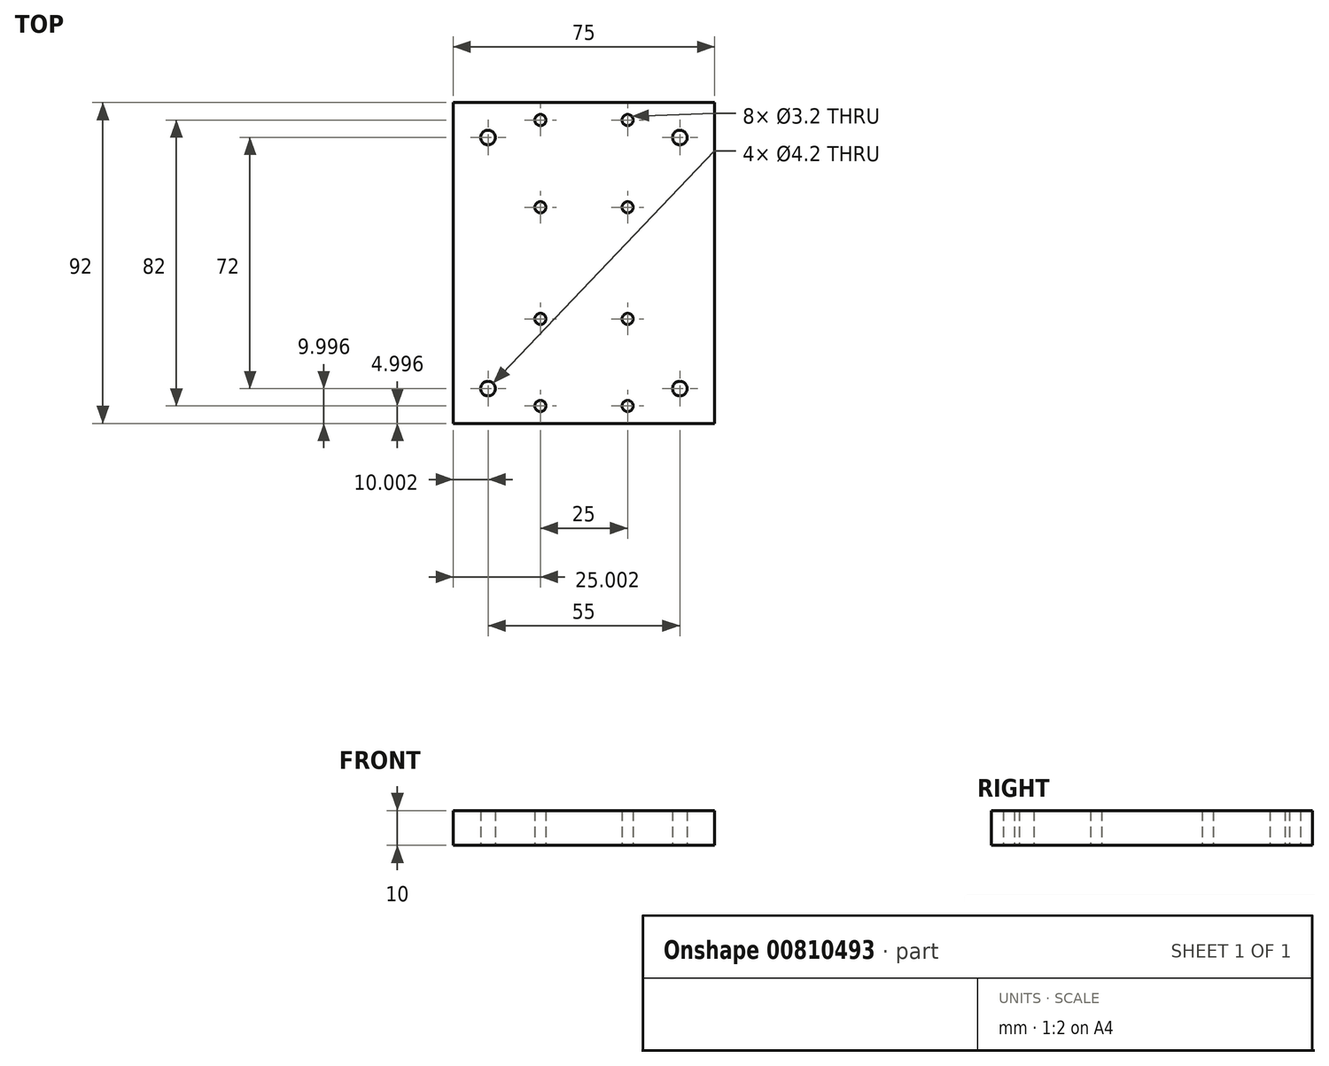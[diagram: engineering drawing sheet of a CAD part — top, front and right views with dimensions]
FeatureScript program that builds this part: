
annotation { "Feature Type Name" : "Feature", "Feature Type Description" : "" }
export const myFeature = defineFeature(function(context is Context, id is Id, definition is map)
    precondition{}
    {
        {
            var Q0;
            Q0=qCreatedBy(makeId("Top.planeOp"),FACE);
            var sketch = newSketch(context, id + "F0", { "sketchPlane" : qUnion([Q0])});
            skLineSegment(sketch, "E0.bottom", {"start": v(-49.76, 39.35) * mm, "end": v(25.24, 39.35) * mm});
            skLineSegment(sketch, "E0.top", {"start": v(-49.76, -52.65) * mm, "end": v(25.24, -52.65) * mm});
            skLineSegment(sketch, "E0.left", {"start": v(-49.76, 39.35) * mm, "end": v(-49.76, -52.65) * mm});
            skLineSegment(sketch, "E0.right", {"start": v(25.24, 39.35) * mm, "end": v(25.24, -52.65) * mm});
            skCircle(sketch, "E1", {"center": v(-39.76, 29.35) * mm, "radius": 2.1 * mm});
            skCircle(sketch, "E2", {"center": v(15.24, 29.35) * mm, "radius": 2.1 * mm});
            skCircle(sketch, "E3", {"center": v(-39.76, -42.65) * mm, "radius": 2.1 * mm});
            skCircle(sketch, "E4", {"center": v(15.24, -42.65) * mm, "radius": 2.1 * mm});
            skCircle(sketch, "E5", {"center": v(0.24, -47.65) * mm, "radius": 1.6 * mm});
            skCircle(sketch, "E6", {"center": v(-24.76, 34.35) * mm, "radius": 1.6 * mm});
            skCircle(sketch, "E7", {"center": v(0.24, 34.35) * mm, "radius": 1.6 * mm});
            skCircle(sketch, "E8", {"center": v(-24.76, 9.35) * mm, "radius": 1.6 * mm});
            skCircle(sketch, "E9", {"center": v(0.24, 9.35) * mm, "radius": 1.6 * mm});
            skCircle(sketch, "E10", {"center": v(-24.76, -47.65) * mm, "radius": 1.6 * mm});
            skCircle(sketch, "E11", {"center": v(-24.76, -22.65) * mm, "radius": 1.6 * mm});
            skCircle(sketch, "E12", {"center": v(0.24, -22.65) * mm, "radius": 1.6 * mm});
            skSolve(sketch);
        }
        {
            var Q0;
            Q0=makeQuery(id+"F0.imprint","IMPRINT",FACE,{"disambiguationData":[TD([[makeQuery(id+"F0.imprint","IMPRINT",EDGE,{"derivedFrom":sQuery(id+"F0.wireOp",EDGE,"E0.bottom")}),-1.0]])]});
            extrude(context, id + "F1", {"entities" : qUnion([Q0]), "depth" : 10 * mm, "offsetDistance" : 25 * mm});
        }
    });
